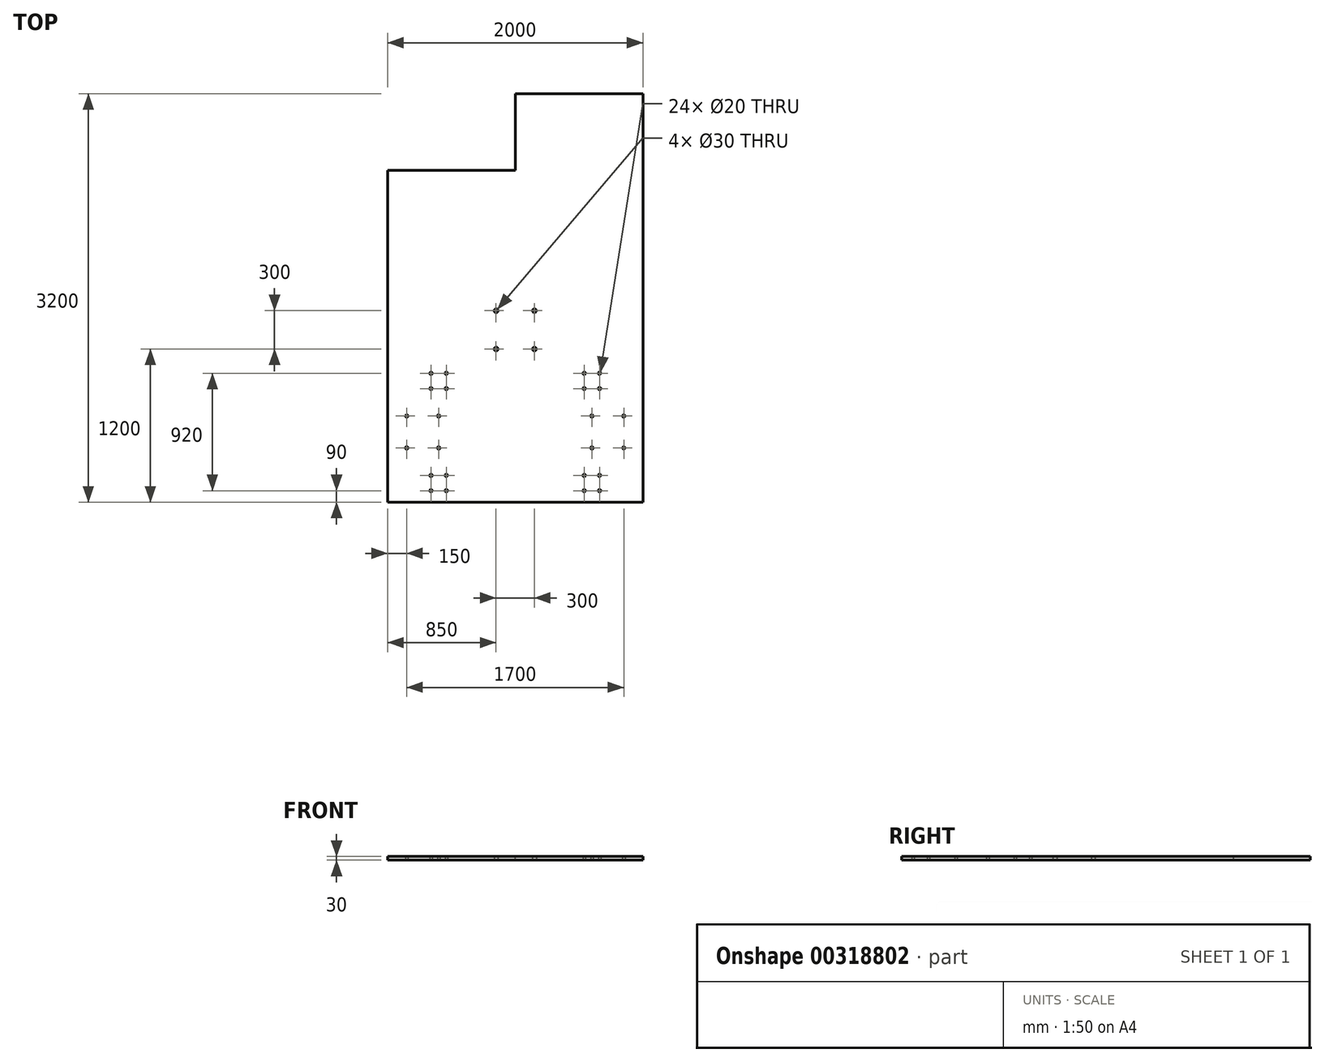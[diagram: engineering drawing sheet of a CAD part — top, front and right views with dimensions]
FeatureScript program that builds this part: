
annotation { "Feature Type Name" : "Feature", "Feature Type Description" : "" }
export const myFeature = defineFeature(function(context is Context, id is Id, definition is map)
    precondition{}
    {
        {
            var Q0;
            Q0=qCreatedBy(makeId("Top.planeOp"),FACE);
            var sketch = newSketch(context, id + "F0", { "sketchPlane" : qUnion([Q0])});
            skLineSegment(sketch, "E0.rect.bottom", {"start": v(-600, -400) * mm, "end": v(600, -400) * mm, "construction": true});
            skLineSegment(sketch, "E0.rect.top", {"start": v(-600, 400) * mm, "end": v(600, 400) * mm, "construction": true});
            skLineSegment(sketch, "E0.rect.left", {"start": v(-600, -400) * mm, "end": v(-600, 400) * mm, "construction": true});
            skLineSegment(sketch, "E0.rect.right", {"start": v(600, -400) * mm, "end": v(600, 400) * mm, "construction": true});
            skPoint(sketch, "E0.rect.middle", {"position": v(0, 0) * mm});
            skLineSegment(sketch, "E1.rect.bottom", {"start": v(-675, 325) * mm, "end": v(-525, 325) * mm, "construction": true});
            skLineSegment(sketch, "E1.rect.top", {"start": v(-675, 475) * mm, "end": v(-525, 475) * mm, "construction": true});
            skLineSegment(sketch, "E1.rect.left", {"start": v(-675, 325) * mm, "end": v(-675, 475) * mm, "construction": true});
            skLineSegment(sketch, "E1.rect.right", {"start": v(-525, 325) * mm, "end": v(-525, 475) * mm, "construction": true});
            skPoint(sketch, "E1.rect.middle", {"position": v(-600, 400) * mm});
            skLineSegment(sketch, "E2.rect.bottom", {"start": v(-660, 340) * mm, "end": v(-540, 340) * mm, "construction": true});
            skLineSegment(sketch, "E2.rect.top", {"start": v(-660, 460) * mm, "end": v(-540, 460) * mm, "construction": true});
            skLineSegment(sketch, "E2.rect.left", {"start": v(-660, 340) * mm, "end": v(-660, 460) * mm, "construction": true});
            skLineSegment(sketch, "E2.rect.right", {"start": v(-540, 340) * mm, "end": v(-540, 460) * mm, "construction": true});
            skCircle(sketch, "E3", {"center": v(-660, 460) * mm, "radius": 10 * mm});
            skCircle(sketch, "E4", {"center": v(-540, 460) * mm, "radius": 10 * mm});
            skCircle(sketch, "E5", {"center": v(-660, 340) * mm, "radius": 10 * mm});
            skCircle(sketch, "E6", {"center": v(-540, 340) * mm, "radius": 10 * mm});
            skCircle(sketch, "E7.MirrorC", {"center": v(660, 460) * mm, "radius": 10 * mm});
            skCircle(sketch, "E8.MirrorC", {"center": v(540, 460) * mm, "radius": 10 * mm});
            skCircle(sketch, "E9.MirrorC", {"center": v(660, 340) * mm, "radius": 10 * mm});
            skCircle(sketch, "E10.MirrorC", {"center": v(540, 340) * mm, "radius": 10 * mm});
            skPoint(sketch, "E11.MirrorP", {"position": v(600, 400) * mm});
            skLineSegment(sketch, "E12.MirrorCS", {"start": v(660, 340) * mm, "end": v(540, 340) * mm, "construction": true});
            skLineSegment(sketch, "E13.MirrorCS", {"start": v(675, 325) * mm, "end": v(525, 325) * mm, "construction": true});
            skLineSegment(sketch, "E14.MirrorCS", {"start": v(675, 475) * mm, "end": v(525, 475) * mm, "construction": true});
            skLineSegment(sketch, "E15.MirrorCS", {"start": v(660, 460) * mm, "end": v(540, 460) * mm, "construction": true});
            skLineSegment(sketch, "E16.MirrorCS", {"start": v(675, 325) * mm, "end": v(675, 475) * mm, "construction": true});
            skLineSegment(sketch, "E17.MirrorCS", {"start": v(525, 325) * mm, "end": v(525, 475) * mm, "construction": true});
            skLineSegment(sketch, "E18.MirrorCS", {"start": v(660, 340) * mm, "end": v(660, 460) * mm, "construction": true});
            skLineSegment(sketch, "E19.MirrorCS", {"start": v(540, 340) * mm, "end": v(540, 460) * mm, "construction": true});
            skCircle(sketch, "E20.MirrorC", {"center": v(660, -340) * mm, "radius": 10 * mm});
            skCircle(sketch, "E21.MirrorC", {"center": v(-660, -340) * mm, "radius": 10 * mm});
            skCircle(sketch, "E22.MirrorC", {"center": v(-540, -460) * mm, "radius": 10 * mm});
            skCircle(sketch, "E23.MirrorC", {"center": v(540, -460) * mm, "radius": 10 * mm});
            skCircle(sketch, "E24.MirrorC", {"center": v(-660, -460) * mm, "radius": 10 * mm});
            skCircle(sketch, "E25.MirrorC", {"center": v(540, -340) * mm, "radius": 10 * mm});
            skCircle(sketch, "E26.MirrorC", {"center": v(-540, -340) * mm, "radius": 10 * mm});
            skCircle(sketch, "E27.MirrorC", {"center": v(660, -460) * mm, "radius": 10 * mm});
            skPoint(sketch, "E28.MirrorP", {"position": v(600, -400) * mm});
            skPoint(sketch, "E29.MirrorP", {"position": v(-600, -400) * mm});
            skLineSegment(sketch, "E30.MirrorCS", {"start": v(-675, -325) * mm, "end": v(-525, -325) * mm, "construction": true});
            skLineSegment(sketch, "E31.MirrorCS", {"start": v(675, -325) * mm, "end": v(525, -325) * mm, "construction": true});
            skLineSegment(sketch, "E32.MirrorCS", {"start": v(675, -325) * mm, "end": v(675, -475) * mm, "construction": true});
            skLineSegment(sketch, "E33.MirrorCS", {"start": v(660, -340) * mm, "end": v(660, -460) * mm, "construction": true});
            skLineSegment(sketch, "E34.MirrorCS", {"start": v(660, -340) * mm, "end": v(540, -340) * mm, "construction": true});
            skLineSegment(sketch, "E35.MirrorCS", {"start": v(675, -475) * mm, "end": v(525, -475) * mm, "construction": true});
            skLineSegment(sketch, "E36.MirrorCS", {"start": v(660, -460) * mm, "end": v(540, -460) * mm, "construction": true});
            skLineSegment(sketch, "E37.MirrorCS", {"start": v(525, -325) * mm, "end": v(525, -475) * mm, "construction": true});
            skLineSegment(sketch, "E38.MirrorCS", {"start": v(540, -340) * mm, "end": v(540, -460) * mm, "construction": true});
            skLineSegment(sketch, "E39.MirrorCS", {"start": v(-525, -325) * mm, "end": v(-525, -475) * mm, "construction": true});
            skLineSegment(sketch, "E40.MirrorCS", {"start": v(-675, -475) * mm, "end": v(-525, -475) * mm, "construction": true});
            skLineSegment(sketch, "E41.MirrorCS", {"start": v(-540, -340) * mm, "end": v(-540, -460) * mm, "construction": true});
            skLineSegment(sketch, "E42.MirrorCS", {"start": v(-660, -340) * mm, "end": v(-660, -460) * mm, "construction": true});
            skLineSegment(sketch, "E43.MirrorCS", {"start": v(-660, -460) * mm, "end": v(-540, -460) * mm, "construction": true});
            skLineSegment(sketch, "E44.MirrorCS", {"start": v(-660, -340) * mm, "end": v(-540, -340) * mm, "construction": true});
            skLineSegment(sketch, "E45.MirrorCS", {"start": v(-675, -325) * mm, "end": v(-675, -475) * mm, "construction": true});
            skLineSegment(sketch, "E46", {"start": v(0, 0) * mm, "end": v(0, 800) * mm, "construction": true});
            skLineSegment(sketch, "E47.rect.bottom", {"start": v(150, 650) * mm, "end": v(-150, 650) * mm, "construction": true});
            skLineSegment(sketch, "E47.rect.top", {"start": v(150, 950) * mm, "end": v(-150, 950) * mm, "construction": true});
            skLineSegment(sketch, "E47.rect.left", {"start": v(150, 650) * mm, "end": v(150, 950) * mm, "construction": true});
            skLineSegment(sketch, "E47.rect.right", {"start": v(-150, 650) * mm, "end": v(-150, 950) * mm, "construction": true});
            skPoint(sketch, "E47.rect.middle", {"position": v(0, 800) * mm});
            skCircle(sketch, "E48", {"center": v(-150, 950) * mm, "radius": 15 * mm});
            skCircle(sketch, "E49", {"center": v(150, 950) * mm, "radius": 15 * mm});
            skCircle(sketch, "E50", {"center": v(150, 650) * mm, "radius": 15 * mm});
            skCircle(sketch, "E51", {"center": v(-150, 650) * mm, "radius": 15 * mm});
            skLineSegment(sketch, "E52.rect.bottom", {"start": v(1000, -550) * mm, "end": v(-1000, -550) * mm});
            skLineSegment(sketch, "E53.top", {"start": v(-1000, 2650) * mm, "end": v(1000, 2650) * mm});
            skLineSegment(sketch, "E54", {"start": v(-1000, 2650) * mm, "end": v(-1000, -550) * mm});
            skLineSegment(sketch, "E55", {"start": v(1000, 2650) * mm, "end": v(1000, -550) * mm});
            skLineSegment(sketch, "E56.bottom", {"start": v(-850, 125) * mm, "end": v(-600, 125) * mm, "construction": true});
            skLineSegment(sketch, "E56.top", {"start": v(-850, -125) * mm, "end": v(-600, -125) * mm, "construction": true});
            skLineSegment(sketch, "E56.left", {"start": v(-850, 125) * mm, "end": v(-850, -125) * mm, "construction": true});
            skLineSegment(sketch, "E56.right", {"start": v(-600, 125) * mm, "end": v(-600, -125) * mm, "construction": true});
            skCircle(sketch, "E57", {"center": v(-600, 125) * mm, "radius": 10 * mm});
            skCircle(sketch, "E58", {"center": v(-850, 125) * mm, "radius": 10 * mm});
            skCircle(sketch, "E59", {"center": v(-850, -125) * mm, "radius": 10 * mm});
            skCircle(sketch, "E60", {"center": v(-600, -125) * mm, "radius": 10 * mm});
            skCircle(sketch, "E61.MirrorC", {"center": v(850, -125) * mm, "radius": 10 * mm});
            skCircle(sketch, "E62.MirrorC", {"center": v(850, 125) * mm, "radius": 10 * mm});
            skCircle(sketch, "E63.MirrorC", {"center": v(600, 125) * mm, "radius": 10 * mm});
            skCircle(sketch, "E64.MirrorC", {"center": v(600, -125) * mm, "radius": 10 * mm});
            skLineSegment(sketch, "E65.MirrorCS", {"start": v(850, 125) * mm, "end": v(850, -125) * mm, "construction": true});
            skLineSegment(sketch, "E66.MirrorCS", {"start": v(850, 125) * mm, "end": v(600, 125) * mm, "construction": true});
            skLineSegment(sketch, "E67.MirrorCS", {"start": v(600, 125) * mm, "end": v(600, -125) * mm, "construction": true});
            skLineSegment(sketch, "E68.MirrorCS", {"start": v(850, -125) * mm, "end": v(600, -125) * mm, "construction": true});
            skLineSegment(sketch, "E69", {"start": v(-600, 125) * mm, "end": v(-850, -125) * mm, "construction": true});
            skLineSegment(sketch, "E70", {"start": v(-600, -125) * mm, "end": v(-850, 125) * mm, "construction": true});
            skPoint(sketch, "E71", {"position": v(-725, 0) * mm});
            skSolve(sketch);
        }
        {
            var Q0;
            Q0=qSketchRegion(id+"F0",true);
            extrude(context, id + "F1", {"entities" : qUnion([Q0]), "depth" : 30 * mm});
        }
        {
            var Q0;
            Q0=makeQuery(id+"F1.opExtrude","CAP_FACE",FACE,{"disambiguationData":[OSD([sQuery(id+"F0.wireOp",EDGE,"E3"),sQuery(id+"F0.wireOp",EDGE,"E4"),sQuery(id+"F0.wireOp",EDGE,"E5"),sQuery(id+"F0.wireOp",EDGE,"E6"),sQuery(id+"F0.wireOp",EDGE,"E7.MirrorC"),sQuery(id+"F0.wireOp",EDGE,"E8.MirrorC"),sQuery(id+"F0.wireOp",EDGE,"E9.MirrorC"),sQuery(id+"F0.wireOp",EDGE,"E10.MirrorC"),sQuery(id+"F0.wireOp",EDGE,"E20.MirrorC"),sQuery(id+"F0.wireOp",EDGE,"E21.MirrorC"),sQuery(id+"F0.wireOp",EDGE,"E22.MirrorC"),sQuery(id+"F0.wireOp",EDGE,"E23.MirrorC"),sQuery(id+"F0.wireOp",EDGE,"E24.MirrorC"),sQuery(id+"F0.wireOp",EDGE,"E25.MirrorC"),sQuery(id+"F0.wireOp",EDGE,"E26.MirrorC"),sQuery(id+"F0.wireOp",EDGE,"E27.MirrorC"),sQuery(id+"F0.wireOp",EDGE,"E48"),sQuery(id+"F0.wireOp",EDGE,"E49"),sQuery(id+"F0.wireOp",EDGE,"E50"),sQuery(id+"F0.wireOp",EDGE,"E51"),sQuery(id+"F0.wireOp",EDGE,"E52.rect.bottom"),sQuery(id+"F0.wireOp",EDGE,"E53.top"),sQuery(id+"F0.wireOp",EDGE,"E54"),sQuery(id+"F0.wireOp",EDGE,"E55")])],"isStart":false});
            var sketch = newSketch(context, id + "F2", { "sketchPlane" : qUnion([Q0])});
            skLineSegment(sketch, "E72.bottom", {"start": v(-1000, 2650) * mm, "end": v(0, 2650) * mm});
            skLineSegment(sketch, "E72.top", {"start": v(-1000, 2050) * mm, "end": v(0, 2050) * mm});
            skLineSegment(sketch, "E72.left", {"start": v(-1000, 2650) * mm, "end": v(-1000, 2050) * mm});
            skLineSegment(sketch, "E72.right", {"start": v(0, 2650) * mm, "end": v(0, 2050) * mm});
            skSolve(sketch);
        }
        {
            var Q0;
            Q0=qSketchRegion(id+"F2",true);
            extrude(context, id + "F3", {"entities" : qUnion([Q0]), "operationType" : NewBodyOperationType.REMOVE, "oppositeDirection" : true, "depth" : 30 * mm});
        }
    });
